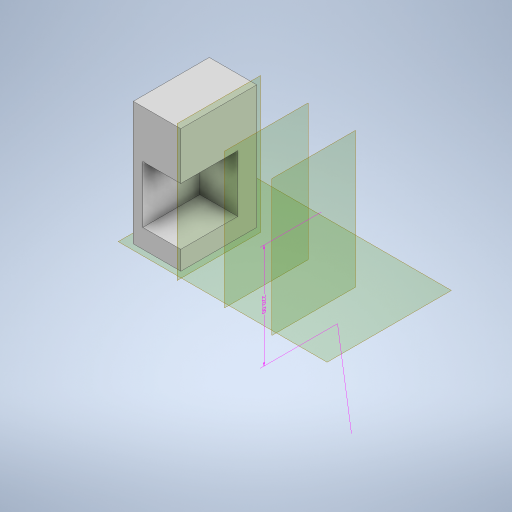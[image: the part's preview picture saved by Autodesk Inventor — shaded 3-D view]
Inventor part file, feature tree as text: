
AUTODESK INVENTOR PART (.ipt)
format: ipt  version: 2023 (Build 270158000, 158)  size: 333,312 bytes
history: native  units: mm
features: extrude x6, plane x6, sketch x6, other x5, split x2
ambient origin geometry x8: Origin, YZ Plane, XZ Plane, XY Plane, X Axis, Y Axis, Z Axis, Center Point
bodies: Body1 (feature_tree), Body2 (feature_tree)
feature tree (25):
  other  "Sólido1"
  other  "Anotaciones"
  extrude  "Extrusión1"  Depth=80.0mm
  extrude  "Extrusión2"  Depth=130.0mm
  extrude  "Extrusión3"  Depth=20.0mm
  extrude  "Extrusión4"  Depth=60.0mm
  plane  "Plano de trabajo1"
  extrude  "Extrusión6"  Depth=20.0mm
  plane  "Plano de trabajo3"
  extrude  "Extrusión7"  [1 undecoded]
  plane  "Plano de trabajo4"
  split  "Dividir1"
  other  "Suprimir cara4"
  plane  "Plano de trabajo5"
  plane  "Plano de trabajo6"
  plane  "Plano de trabajo7"
  split  "Dividir2"
  sketch  "Boceto1"  dims[d0=200.0mm d1=80.0mm]
  sketch  "Boceto2"  dims[d2=130.0mm d3=0.0mm d4=180.0mm]
  sketch  "Boceto3"  dims[d5=60.0mm d6=20.0mm]
  sketch  "Boceto4"  dims[d7=60.0mm d8=0.0mm d9=21.0mm d10=43.0mm]
  sketch  "Boceto7"  dims[d11=43.0mm d12=0.0mm d13=20.0mm]
  other  "Sólido3"
  sketch  "Boceto10"  dims[d14=90.0mm d15=0.0mm d16=-90.0mm d28=20.0mm d29=20.0mm d30=30.0mm d31=30.0mm d32=20.0mm d33=35.0mm d34=35.0mm d35=69.0mm d36=10.0mm d37=0.0mm d45=1.5mm d50=10.0mm d51=0.0mm d52=10.0mm d53=89.5mm d54=90.0deg d38=3.166395mm d39=4.283575mm d40=220.0mm]
  other  "Cota lineal 1"
note: 1 required parameter value undecoded (feature->parameter linkage not recoverable at this tier; creation-order binding heuristic only, values carry confidence <= 0.55)
